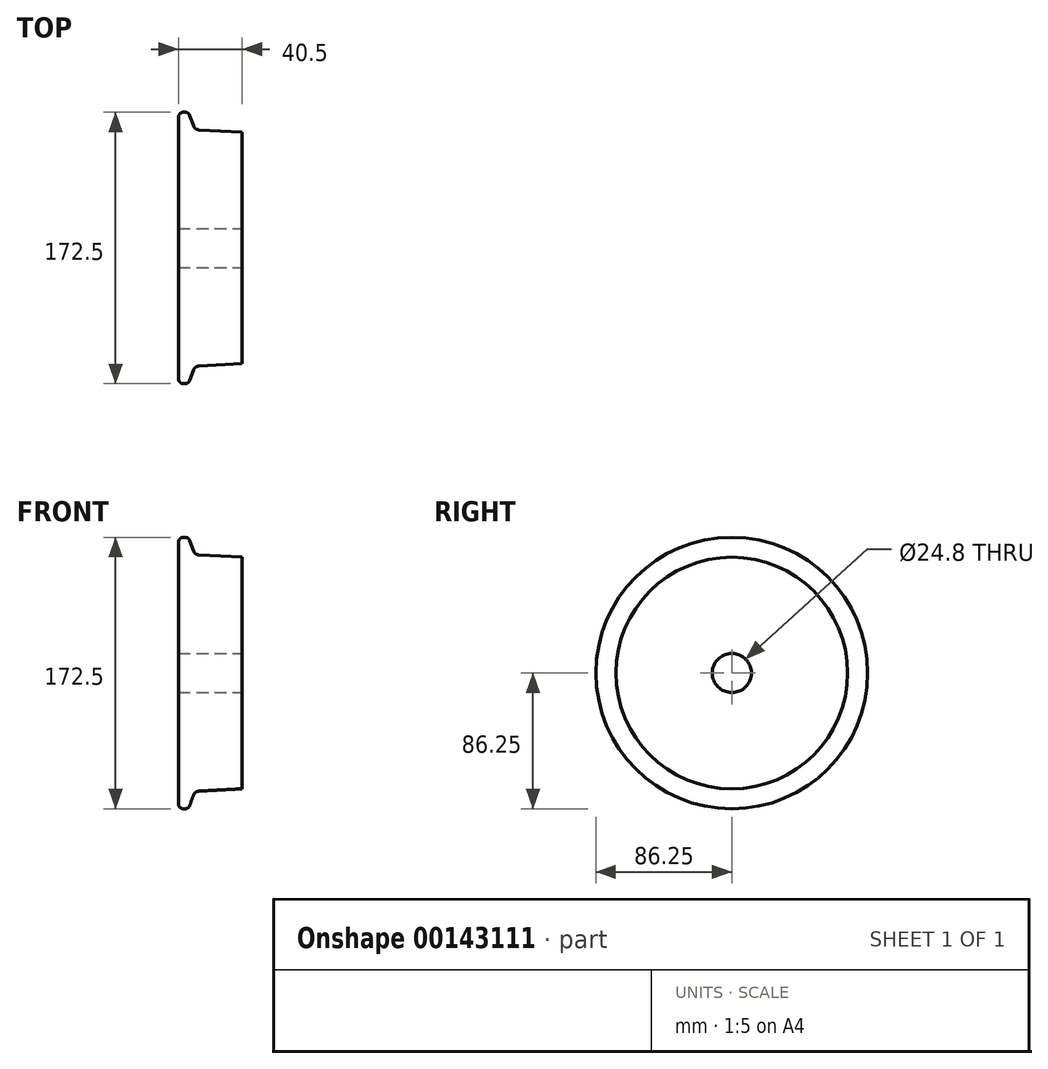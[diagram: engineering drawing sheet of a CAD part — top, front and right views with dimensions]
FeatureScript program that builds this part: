
annotation { "Feature Type Name" : "Feature", "Feature Type Description" : "" }
export const myFeature = defineFeature(function(context is Context, id is Id, definition is map)
    precondition{}
    {
        {
            var Q0;
            Q0=qCreatedBy(makeId("Front.planeOp"),FACE);
            var sketch = newSketch(context, id + "F0", { "sketchPlane" : qUnion([Q0])});
            skLineSegment(sketch, "E0", {"start": v(0, 0) * mm, "end": v(0, 83.07) * mm});
            skLineSegment(sketch, "E1", {"start": v(3.18, 86.25) * mm, "end": v(4.12, 86.25) * mm});
            skLineSegment(sketch, "E2", {"start": v(7.11, 84.16) * mm, "end": v(9.5, 77.6) * mm});
            skLineSegment(sketch, "E3", {"start": v(13.02, 75) * mm, "end": v(40.5, 73.56) * mm});
            skLineSegment(sketch, "E4", {"start": v(40.5, 73.56) * mm, "end": v(40.5, 0) * mm});
            skLineSegment(sketch, "E5", {"start": v(40.5, 0) * mm, "end": v(0, 0) * mm});
            skPoint(sketch, "E6.visualSharp", {"position": v(10.4, 75.14) * mm});
            skArc(sketch, "E6.filletArc", {"start": v(9.5, 77.6) * mm, "mid": v(10.87, 75.77) * mm, "end": v(13.02, 75) * mm});
            skPoint(sketch, "E7.visualSharp", {"position": v(6.35, 86.25) * mm});
            skArc(sketch, "E7.filletArc", {"start": v(7.11, 84.16) * mm, "mid": v(5.95, 85.67) * mm, "end": v(4.12, 86.25) * mm});
            skPoint(sketch, "E8.visualSharp", {"position": v(0, 86.25) * mm});
            skArc(sketch, "E8.filletArc", {"start": v(3.18, 86.25) * mm, "mid": v(0.93, 85.32) * mm, "end": v(0, 83.07) * mm});
            skSolve(sketch);
        }
        {
            var Q0;
            Q0=makeQuery(id+"F0.imprint","IMPRINT",FACE,{"disambiguationData":[TD([[makeQuery(id+"F0.imprint","IMPRINT",EDGE,{"derivedFrom":sQuery(id+"F0.wireOp",EDGE,"E0")}),-1.0]])]});
            var Q1;
            Q1=sQuery(id+"F0.wireOp",EDGE,"E5");
            revolve(context, id + "F1", {"entities" : qUnion([Q0]), "axis" : qUnion([Q1]), "revolveType" : RevolveType.FULL});
        }
        {
            var Q0;
            Q0=makeQuery(id+"F1.opRevolve","SWEPT_FACE",FACE,{"disambiguationData":[OSD([sQuery(id+"F0.wireOp",EDGE,"E4")])]});
            var sketch = newSketch(context, id + "F2", { "sketchPlane" : qUnion([Q0])});
            skCircle(sketch, "E9", {"center": v(0, 0) * mm, "radius": 12.4 * mm});
            skSolve(sketch);
        }
        {
            var Q0;
            Q0=makeQuery(id+"F2.imprint","IMPRINT",FACE,{"disambiguationData":[TD([[makeQuery(id+"F2.imprint","IMPRINT",EDGE,{"derivedFrom":sQuery(id+"F2.wireOp",EDGE,"E9")}),1.0]])]});
            extrude(context, id + "F3", {"entities" : qUnion([Q0]), "operationType" : NewBodyOperationType.REMOVE, "endBound" : BoundingType.THROUGH_ALL, "oppositeDirection" : true, "depth" : 25.4 * mm});
        }
    });
